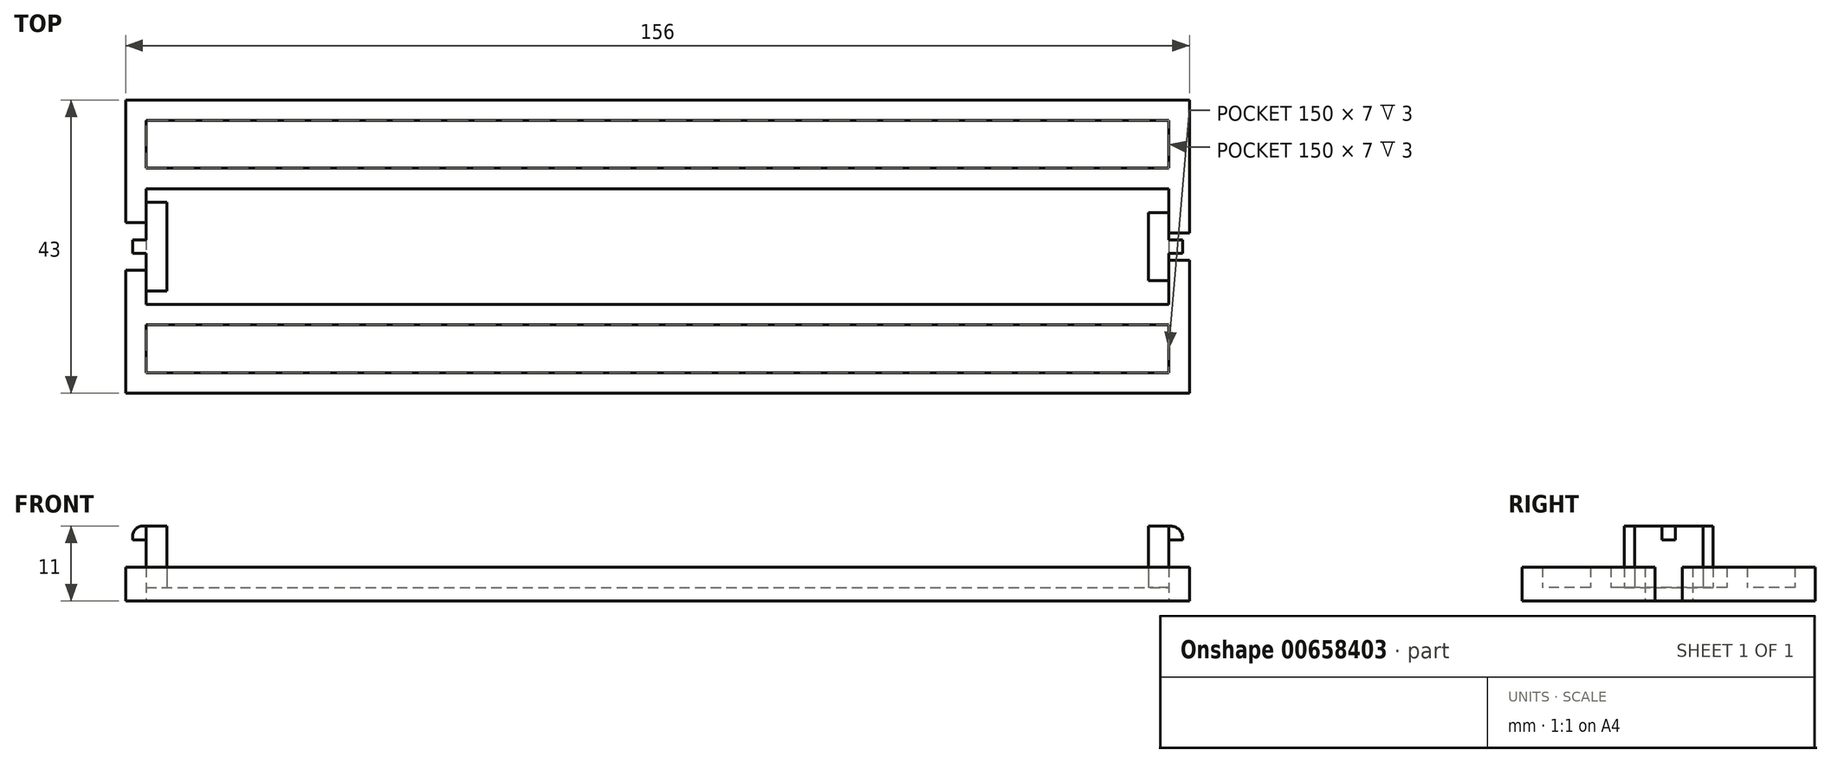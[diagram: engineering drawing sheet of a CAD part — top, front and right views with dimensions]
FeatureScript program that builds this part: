
annotation { "Feature Type Name" : "Feature", "Feature Type Description" : "" }
export const myFeature = defineFeature(function(context is Context, id is Id, definition is map)
    precondition{}
    {
        {
            var Q0;
            Q0=qCreatedBy(makeId("Top.planeOp"),FACE);
            var sketch = newSketch(context, id + "F0", { "sketchPlane" : qUnion([Q0])});
            skLineSegment(sketch, "E0.bottom", {"start": v(-102.86, 19.5) * mm, "end": v(53.14, 19.5) * mm});
            skLineSegment(sketch, "E0.top", {"start": v(-102.86, -23.5) * mm, "end": v(53.14, -23.5) * mm});
            skLineSegment(sketch, "E0.left", {"start": v(-102.86, 19.5) * mm, "end": v(-102.86, -23.5) * mm});
            skLineSegment(sketch, "E0.right", {"start": v(53.14, 19.5) * mm, "end": v(53.14, -23.5) * mm});
            skLineSegment(sketch, "E1", {"start": v(-102.86, -2) * mm, "end": v(53.14, -2) * mm, "construction": true});
            skLineSegment(sketch, "E2", {"start": v(-102.86, 1.5) * mm, "end": v(-99.86, 1.5) * mm});
            skLineSegment(sketch, "E3", {"start": v(-99.86, 1.5) * mm, "end": v(-99.86, -5.5) * mm});
            skLineSegment(sketch, "E4", {"start": v(-99.86, -5.5) * mm, "end": v(-102.86, -5.5) * mm});
            skLineSegment(sketch, "E5", {"start": v(53.14, 0) * mm, "end": v(50.14, 0) * mm});
            skLineSegment(sketch, "E6", {"start": v(50.14, 0) * mm, "end": v(50.14, -4) * mm});
            skLineSegment(sketch, "E7", {"start": v(50.14, -4) * mm, "end": v(53.14, -4) * mm});
            skLineSegment(sketch, "E8.0", {"start": v(50.14, 16.5) * mm, "end": v(50.14, -20.5) * mm});
            skLineSegment(sketch, "E8.1", {"start": v(-99.86, 16.5) * mm, "end": v(50.14, 16.5) * mm});
            skLineSegment(sketch, "E8.2", {"start": v(-99.86, 16.5) * mm, "end": v(-99.86, -20.5) * mm});
            skLineSegment(sketch, "E8.3", {"start": v(-99.86, -20.5) * mm, "end": v(50.14, -20.5) * mm});
            skLineSegment(sketch, "E9", {"start": v(-99.86, -8.5) * mm, "end": v(-96.86, -8.5) * mm});
            skLineSegment(sketch, "E10", {"start": v(-96.86, -8.5) * mm, "end": v(-96.86, 4.5) * mm});
            skLineSegment(sketch, "E11", {"start": v(-96.86, 4.5) * mm, "end": v(-99.86, 4.5) * mm});
            skLineSegment(sketch, "E12", {"start": v(50.14, 3) * mm, "end": v(47.14, 3) * mm});
            skLineSegment(sketch, "E13", {"start": v(47.14, 3) * mm, "end": v(47.14, -7) * mm});
            skLineSegment(sketch, "E14", {"start": v(47.14, -7) * mm, "end": v(50.14, -7) * mm});
            skLineSegment(sketch, "E15.bottom", {"start": v(-99.86, -10.5) * mm, "end": v(50.14, -10.5) * mm});
            skLineSegment(sketch, "E15.top", {"start": v(-99.86, -13.5) * mm, "end": v(50.14, -13.5) * mm});
            skLineSegment(sketch, "E15.left", {"start": v(-99.86, -10.5) * mm, "end": v(-99.86, -13.5) * mm});
            skLineSegment(sketch, "E15.right", {"start": v(50.14, -10.5) * mm, "end": v(50.14, -13.5) * mm});
            skLineSegment(sketch, "E16.MirrorCS", {"start": v(-99.86, 6.5) * mm, "end": v(50.14, 6.5) * mm});
            skLineSegment(sketch, "E17.MirrorCS", {"start": v(-99.86, 9.5) * mm, "end": v(50.14, 9.5) * mm});
            skSolve(sketch);
        }
        {
            var Q0;
            {var subQ8=sQuery(id+"F0.wireOp",EDGE,"E0.bottom");Q0=makeQuery(id+"F0.imprint","IMPRINT",FACE,{"disambiguationData":[TD([[makeQuery(id+"F0.imprint","IMPRINT",EDGE,{"derivedFrom":subQ8}),-1.0]])]});}
            var Q1;
            {var subQ2=sQuery(id+"F0.wireOp",EDGE,"E9");Q1=makeQuery(id+"F0.imprint","IMPRINT",FACE,{"disambiguationData":[TD([[makeQuery(id+"F0.imprint","IMPRINT",EDGE,{"derivedFrom":subQ2}),1.0]])]});}
            var Q2;
            {var subQ5=sQuery(id+"F0.wireOp",EDGE,"E0.top");Q2=makeQuery(id+"F0.imprint","IMPRINT",FACE,{"disambiguationData":[TD([[makeQuery(id+"F0.imprint","IMPRINT",EDGE,{"derivedFrom":subQ5}),1.0]])]});}
            var Q3;
            Q3=makeQuery(id+"F0.imprint","IMPRINT",FACE,{"disambiguationData":[TD([[makeQuery(id+"F0.imprint","IMPRINT",EDGE,{"derivedFrom":sQuery(id+"F0.wireOp",EDGE,"E15.bottom")}),-1.0]])]});
            var Q4;
            {var subQ0=sQuery(id+"F0.wireOp",EDGE,"E16.MirrorCS");Q4=makeQuery(id+"F0.imprint","IMPRINT",FACE,{"disambiguationData":[TD([[makeQuery(id+"F0.imprint","IMPRINT",EDGE,{"derivedFrom":subQ0}),1.0]])]});}
            var Q5;
            {var subQ0=sQuery(id+"F0.wireOp",EDGE,"E12");Q5=makeQuery(id+"F0.imprint","IMPRINT",FACE,{"disambiguationData":[TD([[makeQuery(id+"F0.imprint","IMPRINT",EDGE,{"derivedFrom":subQ0}),1.0]])]});}
            extrude(context, id + "F1", {"entities" : qUnion([Q0, Q1, Q2, Q3, Q4, Q5]), "depth" : 5 * mm, "offsetDistance" : 25 * mm});
        }
        {
            var Q0;
            {var subQ0=sQuery(id+"F0.wireOp",EDGE,"E8.1");Q0=makeQuery(id+"F0.imprint","IMPRINT",FACE,{"disambiguationData":[TD([[makeQuery(id+"F0.imprint","IMPRINT",EDGE,{"derivedFrom":subQ0}),-1.0]])]});}
            var Q1;
            {var subQ3=sQuery(id+"F0.wireOp",EDGE,"E9");Q1=makeQuery(id+"F0.imprint","IMPRINT",FACE,{"disambiguationData":[TD([[makeQuery(id+"F0.imprint","IMPRINT",EDGE,{"derivedFrom":subQ3}),-1.0]])]});}
            var Q2;
            {var subQ0=sQuery(id+"F0.wireOp",EDGE,"E8.3");Q2=makeQuery(id+"F0.imprint","IMPRINT",FACE,{"disambiguationData":[TD([[makeQuery(id+"F0.imprint","IMPRINT",EDGE,{"derivedFrom":subQ0}),1.0]])]});}
            extrude(context, id + "F2", {"entities" : qUnion([Q0, Q1, Q2]), "operationType" : NewBodyOperationType.ADD, "depth" : 2 * mm, "offsetDistance" : 25 * mm});
        }
        {
            var Q0;
            {var subQ2=sQuery(id+"F0.wireOp",EDGE,"E9");Q0=makeQuery(id+"F0.imprint","IMPRINT",FACE,{"disambiguationData":[TD([[makeQuery(id+"F0.imprint","IMPRINT",EDGE,{"derivedFrom":subQ2}),1.0]])]});}
            var Q1;
            {var subQ0=sQuery(id+"F0.wireOp",EDGE,"E12");Q1=makeQuery(id+"F0.imprint","IMPRINT",FACE,{"disambiguationData":[TD([[makeQuery(id+"F0.imprint","IMPRINT",EDGE,{"derivedFrom":subQ0}),1.0]])]});}
            extrude(context, id + "F3", {"entities" : qUnion([Q0, Q1]), "depth" : 11 * mm, "offsetDistance" : 25 * mm});
        }
        {
            var Q0;
            Q0=makeQuery(id+"F1.opExtrude","SWEPT_BODY",BODY,{"disambiguationData":[OSD([sQuery(id+"F0.wireOp",EDGE,"E0.bottom"),sQuery(id+"F0.wireOp",EDGE,"E0.top"),sQuery(id+"F0.wireOp",EDGE,"E0.left"),sQuery(id+"F0.wireOp",EDGE,"E0.right"),sQuery(id+"F0.wireOp",EDGE,"E2"),sQuery(id+"F0.wireOp",EDGE,"E4"),sQuery(id+"F0.wireOp",EDGE,"E5"),sQuery(id+"F0.wireOp",EDGE,"E7"),sQuery(id+"F0.wireOp",EDGE,"E8.0"),sQuery(id+"F0.wireOp",EDGE,"E8.1"),sQuery(id+"F0.wireOp",EDGE,"E8.2"),sQuery(id+"F0.wireOp",EDGE,"E8.3"),sQuery(id+"F0.wireOp",EDGE,"E9"),sQuery(id+"F0.wireOp",EDGE,"E10"),sQuery(id+"F0.wireOp",EDGE,"E11"),sQuery(id+"F0.wireOp",EDGE,"E12"),sQuery(id+"F0.wireOp",EDGE,"E13"),sQuery(id+"F0.wireOp",EDGE,"E14"),sQuery(id+"F0.wireOp",EDGE,"E15.bottom"),sQuery(id+"F0.wireOp",EDGE,"E15.top"),sQuery(id+"F0.wireOp",EDGE,"E16.MirrorCS"),sQuery(id+"F0.wireOp",EDGE,"E17.MirrorCS")])]});
            var Q1;
            Q1=makeQuery(id+"F3.opExtrude","SWEPT_BODY",BODY,{"disambiguationData":[OSD([sQuery(id+"F0.wireOp",EDGE,"E8.0"),sQuery(id+"F0.wireOp",EDGE,"E12"),sQuery(id+"F0.wireOp",EDGE,"E13"),sQuery(id+"F0.wireOp",EDGE,"E14")])]});
            var Q2;
            Q2=makeQuery(id+"F3.opExtrude","SWEPT_BODY",BODY,{"disambiguationData":[OSD([sQuery(id+"F0.wireOp",EDGE,"E8.2"),sQuery(id+"F0.wireOp",EDGE,"E9"),sQuery(id+"F0.wireOp",EDGE,"E10"),sQuery(id+"F0.wireOp",EDGE,"E11")])]});
            booleanBodies(context, id + "F4", {"operationType" : BooleanOperationType.UNION, "tools" : qUnion([Q0, Q1, Q2])});
        }
        {
            var Q0;
            {var subQ0=sQuery(id+"F0.wireOp",EDGE,"E8.2");Q0=makeQuery(id+"F4.opBoolean","MERGE",FACE,{"derivedFrom":[makeQuery(id+"F1.opExtrude","SWEPT_FACE",FACE,{"disambiguationData":[OSD([subQ0]),TDD([makeQuery(id+"F0.imprint","IMPRINT",EDGE,{"disambiguationData":[TD([[makeQuery(id+"F0.imprint","INTERSECT",VERTEX,{"derivedFrom":[sQuery(id+"F0.wireOp",EDGE,"E2"),subQ0]}),-1.0]])],"derivedFrom":subQ0})])]}),makeQuery(id+"F3.opExtrude","SWEPT_FACE",FACE,{"disambiguationData":[OSD([subQ0])]})]});}
            var sketch = newSketch(context, id + "F5", { "sketchPlane" : qUnion([Q0])});
            skLineSegment(sketch, "E18", {"start": v(2, 11) * mm, "end": v(2, 0) * mm, "construction": true});
            skLineSegment(sketch, "E19", {"start": v(1, 11) * mm, "end": v(1, 9) * mm});
            skLineSegment(sketch, "E20", {"start": v(1, 9) * mm, "end": v(3, 9) * mm});
            skLineSegment(sketch, "E21", {"start": v(3, 9) * mm, "end": v(3, 11) * mm});
            skSolve(sketch);
        }
        {
            var Q0;
            {var subQ0=sQuery(id+"F5.wireOp",EDGE,"E19");Q0=makeQuery(id+"F5.imprint","IMPRINT",FACE,{"disambiguationData":[TD([[makeQuery(id+"F5.imprint","IMPRINT",EDGE,{"derivedFrom":subQ0}),1.0]])]});}
            extrude(context, id + "F6", {"entities" : qUnion([Q0]), "operationType" : NewBodyOperationType.ADD, "depth" : 2 * mm, "offsetDistance" : 25 * mm});
        }
        {
            var Q0;
            Q0=makeQuery(id+"F6.opExtrude","CAP_EDGE",EDGE,{"disambiguationData":[OSD([sQuery(id+"F0.wireOp",EDGE,"E8.2")])],"isStart":false});
            fillet(context, id + "F7", {"entities" : qUnion([Q0]), "radius" : 1.5 * mm, "tangentPropagation" : true, "allowEdgeOverflow" : false});
        }
        {
            var Q0;
            {var subQ0=sQuery(id+"F0.wireOp",EDGE,"E8.0");Q0=makeQuery(id+"F4.opBoolean","MERGE",FACE,{"derivedFrom":[makeQuery(id+"F1.opExtrude","SWEPT_FACE",FACE,{"disambiguationData":[OSD([subQ0]),TDD([makeQuery(id+"F0.imprint","IMPRINT",EDGE,{"disambiguationData":[TD([[makeQuery(id+"F0.imprint","INTERSECT",VERTEX,{"derivedFrom":[sQuery(id+"F0.wireOp",EDGE,"E5"),subQ0]}),-1.0]])],"derivedFrom":subQ0})])]}),makeQuery(id+"F3.opExtrude","SWEPT_FACE",FACE,{"disambiguationData":[OSD([subQ0])]})]});}
            var sketch = newSketch(context, id + "F8", { "sketchPlane" : qUnion([Q0])});
            skLineSegment(sketch, "E22.0", {"start": v(-3, 9) * mm, "end": v(-3, 11) * mm});
            skLineSegment(sketch, "E23.0", {"start": v(-1, 9) * mm, "end": v(-3, 9) * mm});
            skLineSegment(sketch, "E24.0", {"start": v(-1, 11) * mm, "end": v(-1, 9) * mm});
            skSolve(sketch);
        }
        {
            var Q0;
            {var subQ0=sQuery(id+"F8.wireOp",EDGE,"E22.0");Q0=makeQuery(id+"F8.imprint","IMPRINT",FACE,{"disambiguationData":[TD([[makeQuery(id+"F8.imprint","IMPRINT",EDGE,{"derivedFrom":subQ0}),-1.0]])]});}
            extrude(context, id + "F9", {"entities" : qUnion([Q0]), "operationType" : NewBodyOperationType.ADD, "depth" : 2 * mm, "offsetDistance" : 25 * mm});
        }
        {
            var Q0;
            Q0=makeQuery(id+"F9.opExtrude","CAP_EDGE",EDGE,{"disambiguationData":[OSD([sQuery(id+"F0.wireOp",EDGE,"E8.0")])],"isStart":false});
            fillet(context, id + "F10", {"entities" : qUnion([Q0]), "radius" : 1.8 * mm, "tangentPropagation" : true, "allowEdgeOverflow" : false});
        }
    });
